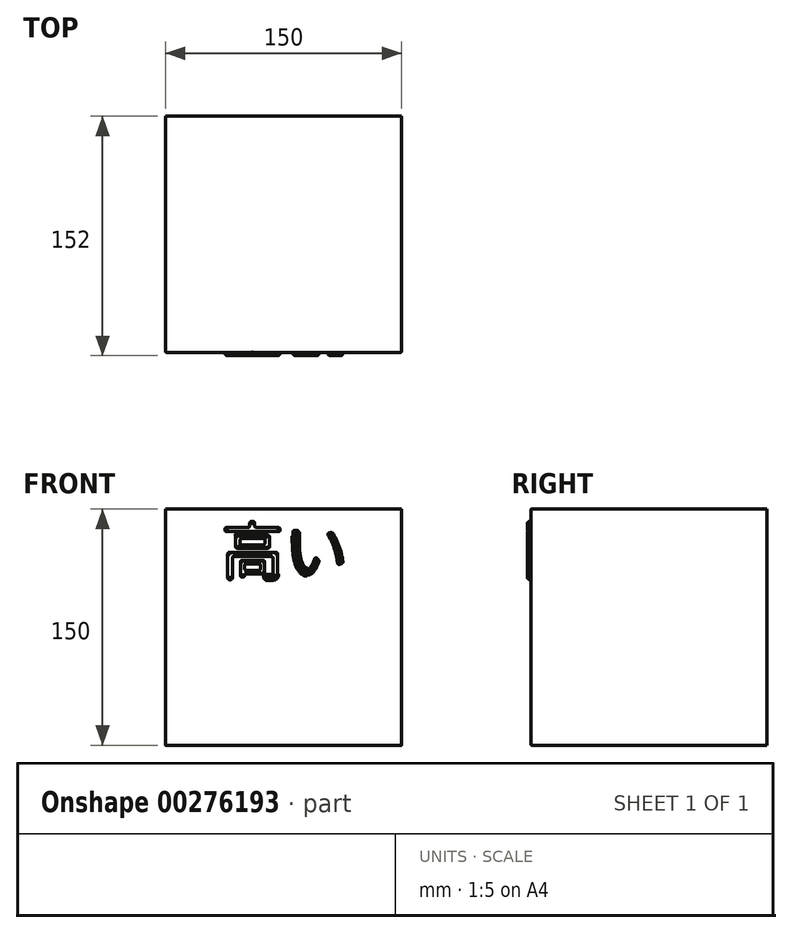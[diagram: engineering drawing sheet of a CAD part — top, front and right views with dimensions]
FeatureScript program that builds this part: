
annotation { "Feature Type Name" : "Feature", "Feature Type Description" : "" }
export const myFeature = defineFeature(function(context is Context, id is Id, definition is map)
    precondition{}
    {
        {
            var Q0;
            Q0=qCreatedBy(makeId("Top.planeOp"),FACE);
            var sketch = newSketch(context, id + "F0", { "sketchPlane" : qUnion([Q0])});
            skLineSegment(sketch, "E0.bottom", {"start": v(-75, 75) * mm, "end": v(75, 75) * mm});
            skLineSegment(sketch, "E0.top", {"start": v(-75, -75) * mm, "end": v(75, -75) * mm});
            skLineSegment(sketch, "E0.left", {"start": v(-75, 75) * mm, "end": v(-75, -75) * mm});
            skLineSegment(sketch, "E0.right", {"start": v(75, 75) * mm, "end": v(75, -75) * mm});
            skPoint(sketch, "E0.middle", {"position": v(0, 0) * mm});
            skSolve(sketch);
        }
        {
            var Q0;
            Q0 = qSketchRegion(id + "F0", true);
            extrude(context, id + "F1", {"entities" : qUnion([Q0]), "depth" : 150 * mm});
        }
        {
            var Q0;
            Q0=makeQuery(id+"F1.opExtrude","SWEPT_FACE",FACE,{"disambiguationData":[OSD([sQuery(id+"F0.wireOp",EDGE,"E0.top")])]});
            var sketch = newSketch(context, id + "F2", { "sketchPlane" : qUnion([Q0])});
            skText(sketch, "E1", { "text": "高い", "fontName": "NotoSansCJKjp-Regular.otf"});
            const initialGuessF2  = {"E1": [-0.04, 0.10822, 1, 0, 0.02921]};
            skSetInitialGuess(sketch, initialGuessF2);
            skSolve(sketch);
        }
        {
            var Q0;
            Q0 = qSketchRegion(id + "F2", true);
            extrude(context, id + "F3", {"entities" : qUnion([Q0]), "operationType" : NewBodyOperationType.ADD, "depth" : 2 * mm});
        }
        {
            var Q0;
            Q0=makeQuery(id+"F3.opExtrude","SWEPT_EDGE",EDGE,{"disambiguationData":[OSD([sQuery(id+"F2.wireOp",EDGE,"E1.sketch_text.stroke-12"),sQuery(id+"F2.wireOp",EDGE,"E1.sketch_text.stroke-13")])]});
            var Q1;
            Q1=makeQuery(id+"F3.opExtrude","SWEPT_EDGE",EDGE,{"disambiguationData":[OSD([sQuery(id+"F2.wireOp",EDGE,"E1.sketch_text.stroke-11"),sQuery(id+"F2.wireOp",EDGE,"E1.sketch_text.stroke-12")])]});
            var Q2;
            Q2=makeQuery(id+"F3.opExtrude","SWEPT_EDGE",EDGE,{"disambiguationData":[OSD([sQuery(id+"F2.wireOp",EDGE,"E1.sketch_text.stroke-6"),sQuery(id+"F2.wireOp",EDGE,"E1.sketch_text.stroke-7")])]});
            var Q3;
            Q3=makeQuery(id+"F3.opExtrude","SWEPT_EDGE",EDGE,{"disambiguationData":[OSD([sQuery(id+"F2.wireOp",EDGE,"E1.sketch_text.stroke-7"),sQuery(id+"F2.wireOp",EDGE,"E1.sketch_text.stroke-8")])]});
            var Q4;
            Q4=makeQuery(id+"F3.opExtrude","SWEPT_EDGE",EDGE,{"disambiguationData":[OSD([sQuery(id+"F2.wireOp",EDGE,"E1.sketch_text.stroke-17"),sQuery(id+"F2.wireOp",EDGE,"E1.sketch_text.stroke-18")])]});
            var Q5;
            Q5=makeQuery(id+"F3.opExtrude","SWEPT_EDGE",EDGE,{"disambiguationData":[OSD([sQuery(id+"F2.wireOp",EDGE,"E1.sketch_text.stroke-18"),sQuery(id+"F2.wireOp",EDGE,"E1.sketch_text.stroke-19")])]});
            var Q6;
            Q6=makeQuery(id+"F3.opExtrude","SWEPT_EDGE",EDGE,{"disambiguationData":[OSD([sQuery(id+"F2.wireOp",EDGE,"E1.sketch_text.stroke-8"),sQuery(id+"F2.wireOp",EDGE,"E1.sketch_text.stroke-9")])]});
            var Q7;
            Q7=makeQuery(id+"F3.opExtrude","SWEPT_EDGE",EDGE,{"disambiguationData":[OSD([sQuery(id+"F2.wireOp",EDGE,"E1.sketch_text.stroke-4"),sQuery(id+"F2.wireOp",EDGE,"E1.sketch_text.stroke-9")])]});
            var Q8;
            Q8=makeQuery(id+"F3.opExtrude","SWEPT_EDGE",EDGE,{"disambiguationData":[OSD([sQuery(id+"F2.wireOp",EDGE,"E1.sketch_text.stroke-4"),sQuery(id+"F2.wireOp",EDGE,"E1.sketch_text.stroke-5")])]});
            var Q9;
            Q9=makeQuery(id+"F3.opExtrude","SWEPT_EDGE",EDGE,{"disambiguationData":[OSD([sQuery(id+"F2.wireOp",EDGE,"E1.sketch_text.stroke-2"),sQuery(id+"F2.wireOp",EDGE,"E1.sketch_text.stroke-3")])]});
            var Q10;
            Q10=makeQuery(id+"F3.opExtrude","SWEPT_EDGE",EDGE,{"disambiguationData":[OSD([sQuery(id+"F2.wireOp",EDGE,"E1.sketch_text.stroke-0"),sQuery(id+"F2.wireOp",EDGE,"E1.sketch_text.stroke-3")])]});
            var Q11;
            Q11=makeQuery(id+"F3.opExtrude","SWEPT_EDGE",EDGE,{"disambiguationData":[OSD([sQuery(id+"F2.wireOp",EDGE,"E1.sketch_text.stroke-0"),sQuery(id+"F2.wireOp",EDGE,"E1.sketch_text.stroke-1")])]});
            var Q12;
            Q12=makeQuery(id+"F3.opExtrude","SWEPT_EDGE",EDGE,{"disambiguationData":[OSD([sQuery(id+"F2.wireOp",EDGE,"E1.sketch_text.stroke-1"),sQuery(id+"F2.wireOp",EDGE,"E1.sketch_text.stroke-2")])]});
            var Q13;
            Q13=makeQuery(id+"F3.opExtrude","SWEPT_EDGE",EDGE,{"disambiguationData":[OSD([sQuery(id+"F2.wireOp",EDGE,"E1.sketch_text.stroke-5"),sQuery(id+"F2.wireOp",EDGE,"E1.sketch_text.stroke-6")])]});
            var Q14;
            Q14=makeQuery(id+"F3.opExtrude","SWEPT_EDGE",EDGE,{"disambiguationData":[OSD([sQuery(id+"F2.wireOp",EDGE,"E1.sketch_text.stroke-10"),sQuery(id+"F2.wireOp",EDGE,"E1.sketch_text.stroke-11")])]});
            var Q15;
            Q15=makeQuery(id+"F3.opExtrude","SWEPT_EDGE",EDGE,{"disambiguationData":[OSD([sQuery(id+"F2.wireOp",EDGE,"E1.sketch_text.stroke-13"),sQuery(id+"F2.wireOp",EDGE,"E1.sketch_text.stroke-14")])]});
            var Q16;
            Q16=makeQuery(id+"F3.opExtrude","SWEPT_EDGE",EDGE,{"disambiguationData":[OSD([sQuery(id+"F2.wireOp",EDGE,"E1.sketch_text.stroke-14"),sQuery(id+"F2.wireOp",EDGE,"E1.sketch_text.stroke-15")])]});
            var Q17;
            Q17=makeQuery(id+"F3.opExtrude","SWEPT_EDGE",EDGE,{"disambiguationData":[OSD([sQuery(id+"F2.wireOp",EDGE,"E1.sketch_text.stroke-10"),sQuery(id+"F2.wireOp",EDGE,"E1.sketch_text.stroke-21")])]});
            var Q18;
            Q18=makeQuery(id+"F3.opExtrude","SWEPT_EDGE",EDGE,{"disambiguationData":[OSD([sQuery(id+"F2.wireOp",EDGE,"E1.sketch_text.stroke-27"),sQuery(id+"F2.wireOp",EDGE,"E1.sketch_text.stroke-28")])]});
            var Q19;
            Q19=makeQuery(id+"F3.opExtrude","SWEPT_EDGE",EDGE,{"disambiguationData":[OSD([sQuery(id+"F2.wireOp",EDGE,"E1.sketch_text.stroke-23"),sQuery(id+"F2.wireOp",EDGE,"E1.sketch_text.stroke-24")])]});
            var Q20;
            Q20=makeQuery(id+"F3.opExtrude","SWEPT_EDGE",EDGE,{"disambiguationData":[OSD([sQuery(id+"F2.wireOp",EDGE,"E1.sketch_text.stroke-26"),sQuery(id+"F2.wireOp",EDGE,"E1.sketch_text.stroke-27")])]});
            var Q21;
            Q21=makeQuery(id+"F3.opExtrude","SWEPT_EDGE",EDGE,{"disambiguationData":[OSD([sQuery(id+"F2.wireOp",EDGE,"E1.sketch_text.stroke-34"),sQuery(id+"F2.wireOp",EDGE,"E1.sketch_text.stroke-35")])]});
            var Q22;
            Q22=makeQuery(id+"F3.opExtrude","SWEPT_EDGE",EDGE,{"disambiguationData":[OSD([sQuery(id+"F2.wireOp",EDGE,"E1.sketch_text.stroke-22"),sQuery(id+"F2.wireOp",EDGE,"E1.sketch_text.stroke-25")])]});
            var Q23;
            Q23=makeQuery(id+"F3.opExtrude","SWEPT_EDGE",EDGE,{"disambiguationData":[OSD([sQuery(id+"F2.wireOp",EDGE,"E1.sketch_text.stroke-28"),sQuery(id+"F2.wireOp",EDGE,"E1.sketch_text.stroke-29")])]});
            var Q24;
            Q24=makeQuery(id+"F3.opExtrude","SWEPT_EDGE",EDGE,{"disambiguationData":[OSD([sQuery(id+"F2.wireOp",EDGE,"E1.sketch_text.stroke-33"),sQuery(id+"F2.wireOp",EDGE,"E1.sketch_text.stroke-34")])]});
            var Q25;
            Q25=makeQuery(id+"F3.opExtrude","SWEPT_EDGE",EDGE,{"disambiguationData":[OSD([sQuery(id+"F2.wireOp",EDGE,"E1.sketch_text.stroke-32"),sQuery(id+"F2.wireOp",EDGE,"E1.sketch_text.stroke-33")])]});
            var Q26;
            Q26=makeQuery(id+"F3.opExtrude","SWEPT_EDGE",EDGE,{"disambiguationData":[OSD([sQuery(id+"F2.wireOp",EDGE,"E1.sketch_text.stroke-31"),sQuery(id+"F2.wireOp",EDGE,"E1.sketch_text.stroke-32")])]});
            var Q27;
            Q27=makeQuery(id+"F3.opExtrude","SWEPT_EDGE",EDGE,{"disambiguationData":[OSD([sQuery(id+"F2.wireOp",EDGE,"E1.sketch_text.stroke-30"),sQuery(id+"F2.wireOp",EDGE,"E1.sketch_text.stroke-31")])]});
            var Q28;
            Q28=makeQuery(id+"F3.opExtrude","SWEPT_EDGE",EDGE,{"disambiguationData":[OSD([sQuery(id+"F2.wireOp",EDGE,"E1.sketch_text.stroke-30"),sQuery(id+"F2.wireOp",EDGE,"E1.sketch_text.stroke-37")])]});
            var Q29;
            Q29=makeQuery(id+"F3.opExtrude","SWEPT_EDGE",EDGE,{"disambiguationData":[OSD([sQuery(id+"F2.wireOp",EDGE,"E1.sketch_text.stroke-36"),sQuery(id+"F2.wireOp",EDGE,"E1.sketch_text.stroke-37")])]});
            var Q30;
            Q30=makeQuery(id+"F3.opExtrude","SWEPT_EDGE",EDGE,{"disambiguationData":[OSD([sQuery(id+"F2.wireOp",EDGE,"E1.sketch_text.stroke-35"),sQuery(id+"F2.wireOp",EDGE,"E1.sketch_text.stroke-36")])]});
            var Q31;
            Q31=makeQuery(id+"F3.opExtrude","SWEPT_EDGE",EDGE,{"disambiguationData":[OSD([sQuery(id+"F2.wireOp",EDGE,"E1.sketch_text.stroke-38"),sQuery(id+"F2.wireOp",EDGE,"E1.sketch_text.stroke-39")])]});
            var Q32;
            Q32=makeQuery(id+"F3.opExtrude","SWEPT_EDGE",EDGE,{"disambiguationData":[OSD([sQuery(id+"F2.wireOp",EDGE,"E1.sketch_text.stroke-38"),sQuery(id+"F2.wireOp",EDGE,"E1.sketch_text.stroke-47")])]});
            var Q33;
            Q33=makeQuery(id+"F3.opExtrude","SWEPT_EDGE",EDGE,{"disambiguationData":[OSD([sQuery(id+"F2.wireOp",EDGE,"E1.sketch_text.stroke-43"),sQuery(id+"F2.wireOp",EDGE,"E1.sketch_text.stroke-44")])]});
            var Q34;
            Q34=makeQuery(id+"F3.opExtrude","SWEPT_EDGE",EDGE,{"disambiguationData":[OSD([sQuery(id+"F2.wireOp",EDGE,"E1.sketch_text.stroke-42"),sQuery(id+"F2.wireOp",EDGE,"E1.sketch_text.stroke-43")])]});
            var Q35;
            Q35=makeQuery(id+"F3.opExtrude","SWEPT_EDGE",EDGE,{"disambiguationData":[OSD([sQuery(id+"F2.wireOp",EDGE,"E1.sketch_text.stroke-48"),sQuery(id+"F2.wireOp",EDGE,"E1.sketch_text.stroke-49")])]});
            var Q36;
            Q36=makeQuery(id+"F3.opExtrude","SWEPT_EDGE",EDGE,{"disambiguationData":[OSD([sQuery(id+"F2.wireOp",EDGE,"E1.sketch_text.stroke-48"),sQuery(id+"F2.wireOp",EDGE,"E1.sketch_text.stroke-51")])]});
            var Q37;
            Q37=makeQuery(id+"F3.opExtrude","SWEPT_EDGE",EDGE,{"disambiguationData":[OSD([sQuery(id+"F2.wireOp",EDGE,"E1.sketch_text.stroke-49"),sQuery(id+"F2.wireOp",EDGE,"E1.sketch_text.stroke-50")])]});
            var Q38;
            Q38=makeQuery(id+"F3.opExtrude","SWEPT_EDGE",EDGE,{"disambiguationData":[OSD([sQuery(id+"F2.wireOp",EDGE,"E1.sketch_text.stroke-50"),sQuery(id+"F2.wireOp",EDGE,"E1.sketch_text.stroke-51")])]});
            fillet(context, id + "F4", {"entities" : qUnion([Q0, Q1, Q2, Q3, Q4, Q5, Q6, Q7, Q8, Q9, Q10, Q11, Q12, Q13, Q14, Q15, Q16, Q17, Q18, Q19, Q20, Q21, Q22, Q23, Q24, Q25, Q26, Q27, Q28, Q29, Q30, Q31, Q32, Q33, Q34, Q35, Q36, Q37, Q38]), "radius" : 1 * mm, "allowEdgeOverflow" : false});
        }
        {
            var Q0;
            Q0=makeQuery(id+"F3.opExtrude","CAP_FACE",FACE,{"disambiguationData":[OSD([sQuery(id+"F2.wireOp",EDGE,"E1.sketch_text.stroke-10"),sQuery(id+"F2.wireOp",EDGE,"E1.sketch_text.stroke-11"),sQuery(id+"F2.wireOp",EDGE,"E1.sketch_text.stroke-12"),sQuery(id+"F2.wireOp",EDGE,"E1.sketch_text.stroke-13"),sQuery(id+"F2.wireOp",EDGE,"E1.sketch_text.stroke-14"),sQuery(id+"F2.wireOp",EDGE,"E1.sketch_text.stroke-15"),sQuery(id+"F2.wireOp",EDGE,"E1.sketch_text.stroke-16"),sQuery(id+"F2.wireOp",EDGE,"E1.sketch_text.stroke-17"),sQuery(id+"F2.wireOp",EDGE,"E1.sketch_text.stroke-18"),sQuery(id+"F2.wireOp",EDGE,"E1.sketch_text.stroke-19"),sQuery(id+"F2.wireOp",EDGE,"E1.sketch_text.stroke-20"),sQuery(id+"F2.wireOp",EDGE,"E1.sketch_text.stroke-21")])],"isStart":false});
            var Q1;
            Q1=makeQuery(id+"F3.opExtrude","CAP_FACE",FACE,{"disambiguationData":[OSD([sQuery(id+"F2.wireOp",EDGE,"E1.sketch_text.stroke-0"),sQuery(id+"F2.wireOp",EDGE,"E1.sketch_text.stroke-1"),sQuery(id+"F2.wireOp",EDGE,"E1.sketch_text.stroke-2"),sQuery(id+"F2.wireOp",EDGE,"E1.sketch_text.stroke-3"),sQuery(id+"F2.wireOp",EDGE,"E1.sketch_text.stroke-4"),sQuery(id+"F2.wireOp",EDGE,"E1.sketch_text.stroke-5"),sQuery(id+"F2.wireOp",EDGE,"E1.sketch_text.stroke-6"),sQuery(id+"F2.wireOp",EDGE,"E1.sketch_text.stroke-7"),sQuery(id+"F2.wireOp",EDGE,"E1.sketch_text.stroke-8"),sQuery(id+"F2.wireOp",EDGE,"E1.sketch_text.stroke-9")])],"isStart":false});
            var Q2;
            Q2=makeQuery(id+"F3.opExtrude","CAP_FACE",FACE,{"disambiguationData":[OSD([sQuery(id+"F2.wireOp",EDGE,"E1.sketch_text.stroke-38"),sQuery(id+"F2.wireOp",EDGE,"E1.sketch_text.stroke-39"),sQuery(id+"F2.wireOp",EDGE,"E1.sketch_text.stroke-40"),sQuery(id+"F2.wireOp",EDGE,"E1.sketch_text.stroke-41"),sQuery(id+"F2.wireOp",EDGE,"E1.sketch_text.stroke-42"),sQuery(id+"F2.wireOp",EDGE,"E1.sketch_text.stroke-43"),sQuery(id+"F2.wireOp",EDGE,"E1.sketch_text.stroke-44"),sQuery(id+"F2.wireOp",EDGE,"E1.sketch_text.stroke-45"),sQuery(id+"F2.wireOp",EDGE,"E1.sketch_text.stroke-46"),sQuery(id+"F2.wireOp",EDGE,"E1.sketch_text.stroke-47")])],"isStart":false});
            var Q3;
            Q3=makeQuery(id+"F3.opExtrude","CAP_FACE",FACE,{"disambiguationData":[OSD([sQuery(id+"F2.wireOp",EDGE,"E1.sketch_text.stroke-48"),sQuery(id+"F2.wireOp",EDGE,"E1.sketch_text.stroke-49"),sQuery(id+"F2.wireOp",EDGE,"E1.sketch_text.stroke-50"),sQuery(id+"F2.wireOp",EDGE,"E1.sketch_text.stroke-51")])],"isStart":false});
            var Q4;
            Q4=makeQuery(id+"F3.opExtrude","CAP_FACE",FACE,{"disambiguationData":[OSD([sQuery(id+"F2.wireOp",EDGE,"E1.sketch_text.stroke-22"),sQuery(id+"F2.wireOp",EDGE,"E1.sketch_text.stroke-23"),sQuery(id+"F2.wireOp",EDGE,"E1.sketch_text.stroke-24"),sQuery(id+"F2.wireOp",EDGE,"E1.sketch_text.stroke-25"),sQuery(id+"F2.wireOp",EDGE,"E1.sketch_text.stroke-26"),sQuery(id+"F2.wireOp",EDGE,"E1.sketch_text.stroke-27"),sQuery(id+"F2.wireOp",EDGE,"E1.sketch_text.stroke-28"),sQuery(id+"F2.wireOp",EDGE,"E1.sketch_text.stroke-29")])],"isStart":false});
            var Q5;
            Q5=makeQuery(id+"F3.opExtrude","CAP_FACE",FACE,{"disambiguationData":[OSD([sQuery(id+"F2.wireOp",EDGE,"E1.sketch_text.stroke-30"),sQuery(id+"F2.wireOp",EDGE,"E1.sketch_text.stroke-31"),sQuery(id+"F2.wireOp",EDGE,"E1.sketch_text.stroke-32"),sQuery(id+"F2.wireOp",EDGE,"E1.sketch_text.stroke-33"),sQuery(id+"F2.wireOp",EDGE,"E1.sketch_text.stroke-34"),sQuery(id+"F2.wireOp",EDGE,"E1.sketch_text.stroke-35"),sQuery(id+"F2.wireOp",EDGE,"E1.sketch_text.stroke-36"),sQuery(id+"F2.wireOp",EDGE,"E1.sketch_text.stroke-37")])],"isStart":false});
            fillet(context, id + "F5", {"entities" : qUnion([Q0, Q1, Q2, Q3, Q4, Q5]), "radius" : 1.31 * mm, "tangentPropagation" : true, "allowEdgeOverflow" : false});
        }
        {
            var Q0;
            {var subQ1=sQuery(id+"F0.wireOp",EDGE,"E0.left");var subQ2=sQuery(id+"F0.wireOp",EDGE,"E0.top");Q0=makeQuery(id+"F3.boolean.opBoolean","SPLIT",FACE,{"disambiguationData":[TD([makeQuery(id+"F1.opExtrude","SWEPT_FACE",FACE,{"disambiguationData":[OSD([subQ1])]})])],"derivedFrom":makeQuery(id+"F1.opExtrude","SWEPT_FACE",FACE,{"disambiguationData":[OSD([subQ2])]})});}
            fillet(context, id + "F6", {"entities" : qUnion([Q0]), "radius" : .6 * mm, "tangentPropagation" : true, "allowEdgeOverflow" : false});
        }
    });
